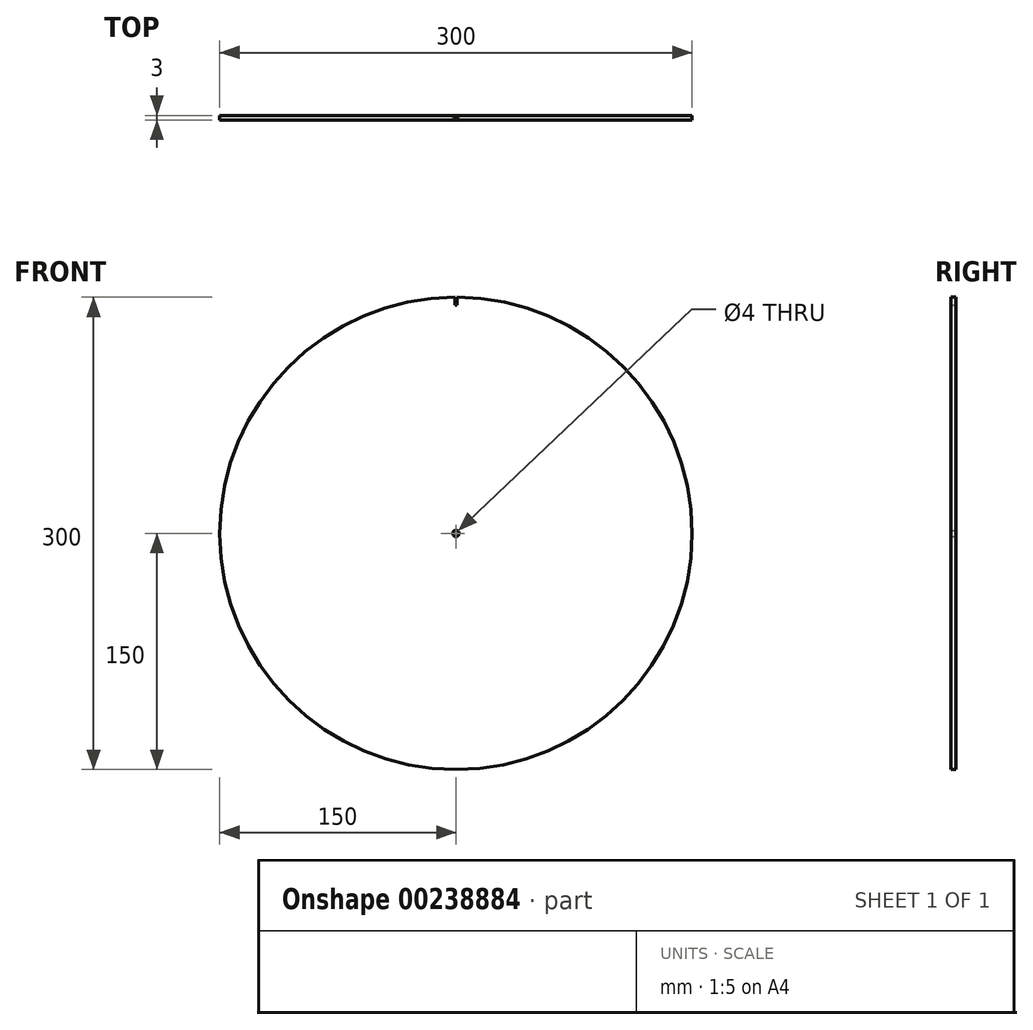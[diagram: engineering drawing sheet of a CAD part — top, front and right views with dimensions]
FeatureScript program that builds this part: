
annotation { "Feature Type Name" : "Feature", "Feature Type Description" : "" }
export const myFeature = defineFeature(function(context is Context, id is Id, definition is map)
    precondition{}
    {
        {
            var Q0;
            Q0=qCreatedBy(makeId("Front.planeOp"),FACE);
            var sketch = newSketch(context, id + "F0", { "sketchPlane" : qUnion([Q0])});
            skCircle(sketch, "E0", {"center": v(0, 0) * mm, "radius": 150 * mm});
            skCircle(sketch, "E1", {"center": v(0, 0) * mm, "radius": 2 * mm});
            skSolve(sketch);
        }
        {
            var Q0;
            Q0 = qSketchRegion(id + "F0", true);
            extrude(context, id + "F1", {"entities" : qUnion([Q0]), "depth" : 3 * mm});
        }
        {
            var Q0;
            Q0=qCreatedBy(makeId("Front.planeOp"),FACE);
            var sketch = newSketch(context, id + "F2", { "sketchPlane" : qUnion([Q0])});
            skLineSegment(sketch, "E2", {"start": v(0, 0) * mm, "end": v(0, 166.14) * mm, "construction": true});
            skLineSegment(sketch, "E3.bottom", {"start": v(-0.5, 151.12) * mm, "end": v(0.5, 151.12) * mm});
            skLineSegment(sketch, "E3.top", {"start": v(-0.5, 145) * mm, "end": v(0.5, 145) * mm});
            skLineSegment(sketch, "E3.left", {"start": v(-0.5, 151.12) * mm, "end": v(-0.5, 145) * mm});
            skLineSegment(sketch, "E3.right", {"start": v(0.5, 151.12) * mm, "end": v(0.5, 145) * mm});
            skSolve(sketch);
        }
        {
            var Q0;
            Q0 = qSketchRegion(id + "F2", true);
            extrude(context, id + "F3", {"entities" : qUnion([Q0]), "operationType" : NewBodyOperationType.REMOVE, "depth" : 18.2 * mm});
        }
    });
